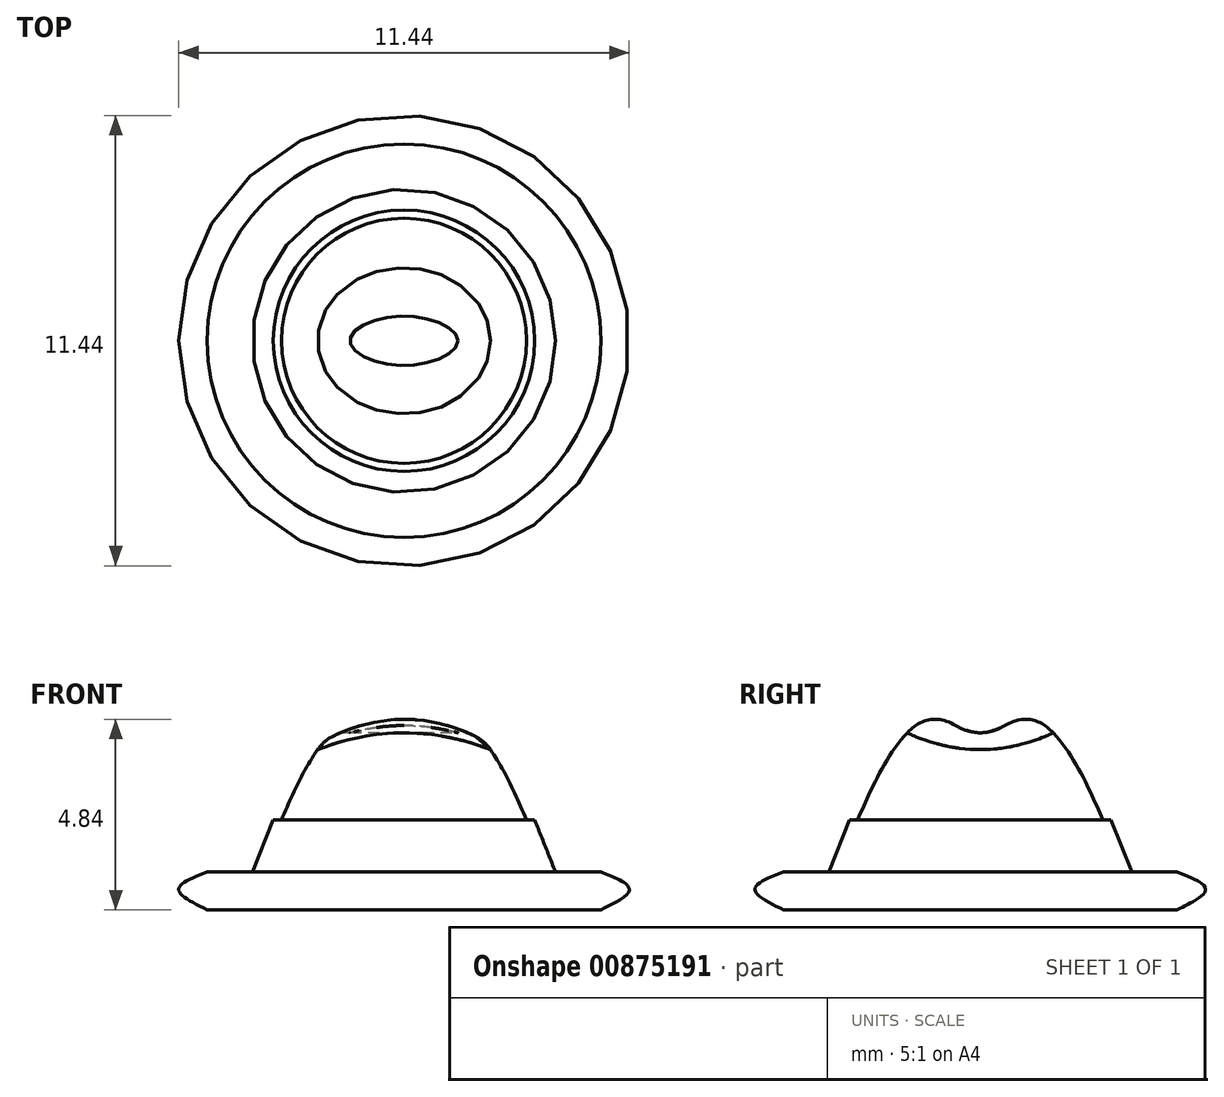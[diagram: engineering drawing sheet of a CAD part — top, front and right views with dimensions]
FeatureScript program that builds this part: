
annotation { "Feature Type Name" : "Feature", "Feature Type Description" : "" }
export const myFeature = defineFeature(function(context is Context, id is Id, definition is map)
    precondition{}
    {
        {
            var Q0;
            Q0=qCreatedBy(makeId("Front.planeOp"),FACE);
            var sketch = newSketch(context, id + "F0", { "sketchPlane" : qUnion([Q0])});
            skFitSpline(sketch, "E0", {"points": [v(0, 18.04) * mm, v(0.98, 18.43) * mm, v(2.14, 17.58) * mm, v(3.63, 14.4) * mm], "startDerivative": vector(4.54, 0.8) * mm, "endDerivative": vector(3.07, -8) * mm});
            skLineSegment(sketch, "E1", {"start": v(3.63, 14.4) * mm, "end": v(5, 14.4) * mm});
            skFitSpline(sketch, "E2", {"points": [v(5, 14.4) * mm, v(5.72, 13.96) * mm, v(5, 13.44) * mm], "startDerivative": vector(2.18, -0.86) * mm, "endDerivative": vector(-2.16, -1.07) * mm});
            skLineSegment(sketch, "E3", {"start": v(5, 13.44) * mm, "end": v(0, 13.44) * mm});
            skLineSegment(sketch, "E4", {"start": v(0, 13.44) * mm, "end": v(0, 18.04) * mm});
            skSolve(sketch);
        }
        {
            var Q0;
            Q0=makeQuery(id+"F0.imprint","IMPRINT",FACE,{"disambiguationData":[TD([[makeQuery(id+"F0.imprint","IMPRINT",EDGE,{"derivedFrom":sQuery(id+"F0.wireOp",EDGE,"E0")}),-1.0]])]});
            var Q1;
            Q1=sQuery(id+"F0.wireOp",EDGE,"E4");
            revolve(context, id + "F1", {"surfaceOperationType" : NewSurfaceOperationType.NEW, "entities" : qUnion([Q0]), "axis" : qUnion([Q1]), "revolveType" : RevolveType.FULL});
        }
        {
            var Q0;
            Q0=qCreatedBy(makeId("Front.planeOp"),FACE);
            var sketch = newSketch(context, id + "F2", { "sketchPlane" : qUnion([Q0])});
            skLineSegment(sketch, "E5", {"start": v(3.32, 15.72) * mm, "end": v(0, 15.72) * mm});
            skLineSegment(sketch, "E6", {"start": v(0, 15.72) * mm, "end": v(0, 14.4) * mm});
            skLineSegment(sketch, "E7", {"start": v(0, 14.4) * mm, "end": v(3.85, 14.4) * mm});
            skLineSegment(sketch, "E8", {"start": v(3.85, 14.4) * mm, "end": v(3.32, 15.72) * mm});
            skLineSegment(sketch, "E9", {"start": v(0, 14.4) * mm, "end": v(0, 15.72) * mm});
            skSolve(sketch);
        }
        {
            var Q0;
            Q0=makeQuery(id+"F2.imprint","IMPRINT",FACE,{"disambiguationData":[TD([[makeQuery(id+"F2.imprint","IMPRINT",EDGE,{"derivedFrom":sQuery(id+"F2.wireOp",EDGE,"E5")}),1.0]])]});
            var Q1;
            Q1=sQuery(id+"F2.wireOp",EDGE,"E6");
            revolve(context, id + "F3", {"operationType" : NewBodyOperationType.ADD, "surfaceOperationType" : NewSurfaceOperationType.NEW, "entities" : qUnion([Q0]), "axis" : qUnion([Q1]), "revolveType" : RevolveType.FULL});
        }
        {
            var Q0;
            Q0=qCreatedBy(makeId("Right.planeOp"),FACE);
            var sketch = newSketch(context, id + "F4", { "sketchPlane" : qUnion([Q0])});
            skLineSegment(sketch, "E10", {"start": v(-3.05, 21.09) * mm, "end": v(0, 21.09) * mm});
            skLineSegment(sketch, "E11.MirrorCS", {"start": v(3.05, 21.09) * mm, "end": v(0, 21.09) * mm});
            skFitSpline(sketch, "E12", {"points": [v(-3.05, 21.09) * mm, v(0, 17.94) * mm, v(3.05, 21.09) * mm], "startDerivative": vector(6.1, -9.44) * mm, "endDerivative": vector(6.1, 9.44) * mm});
            skSolve(sketch);
        }
        {
            var Q0;
            Q0=makeQuery(id+"F4.imprint","IMPRINT",FACE,{"disambiguationData":[TD([[makeQuery(id+"F4.imprint","IMPRINT",EDGE,{"derivedFrom":sQuery(id+"F4.wireOp",EDGE,"E10")}),-1.0]])]});
            extrude(context, id + "F5", {"entities" : qUnion([Q0]), "operationType" : NewBodyOperationType.REMOVE, "endBound" : BoundingType.SYMMETRIC, "depth" : 21.9 * mm, "offsetDistance" : 25 * mm});
        }
        {
            var Q0;
            Q0=makeQuery(id+"F5.boolean.opBoolean","INTERSECT",EDGE,{"derivedFrom":[makeQuery(id+"F1.opRevolve","SWEPT_FACE",FACE,{"disambiguationData":[OSD([sQuery(id+"F0.wireOp",EDGE,"E0")])]}),makeQuery(id+"F5.opExtrude","SWEPT_FACE",FACE,{"disambiguationData":[OSD([sQuery(id+"F4.wireOp",EDGE,"E12")])]})]});
            fillet(context, id + "F6", {"entities" : qUnion([Q0]), "radius" : 1 * mm, "rho" : 0.5, "crossSection" : FilletCrossSection.CONIC, "allowEdgeOverflow" : false});
        }
    });
